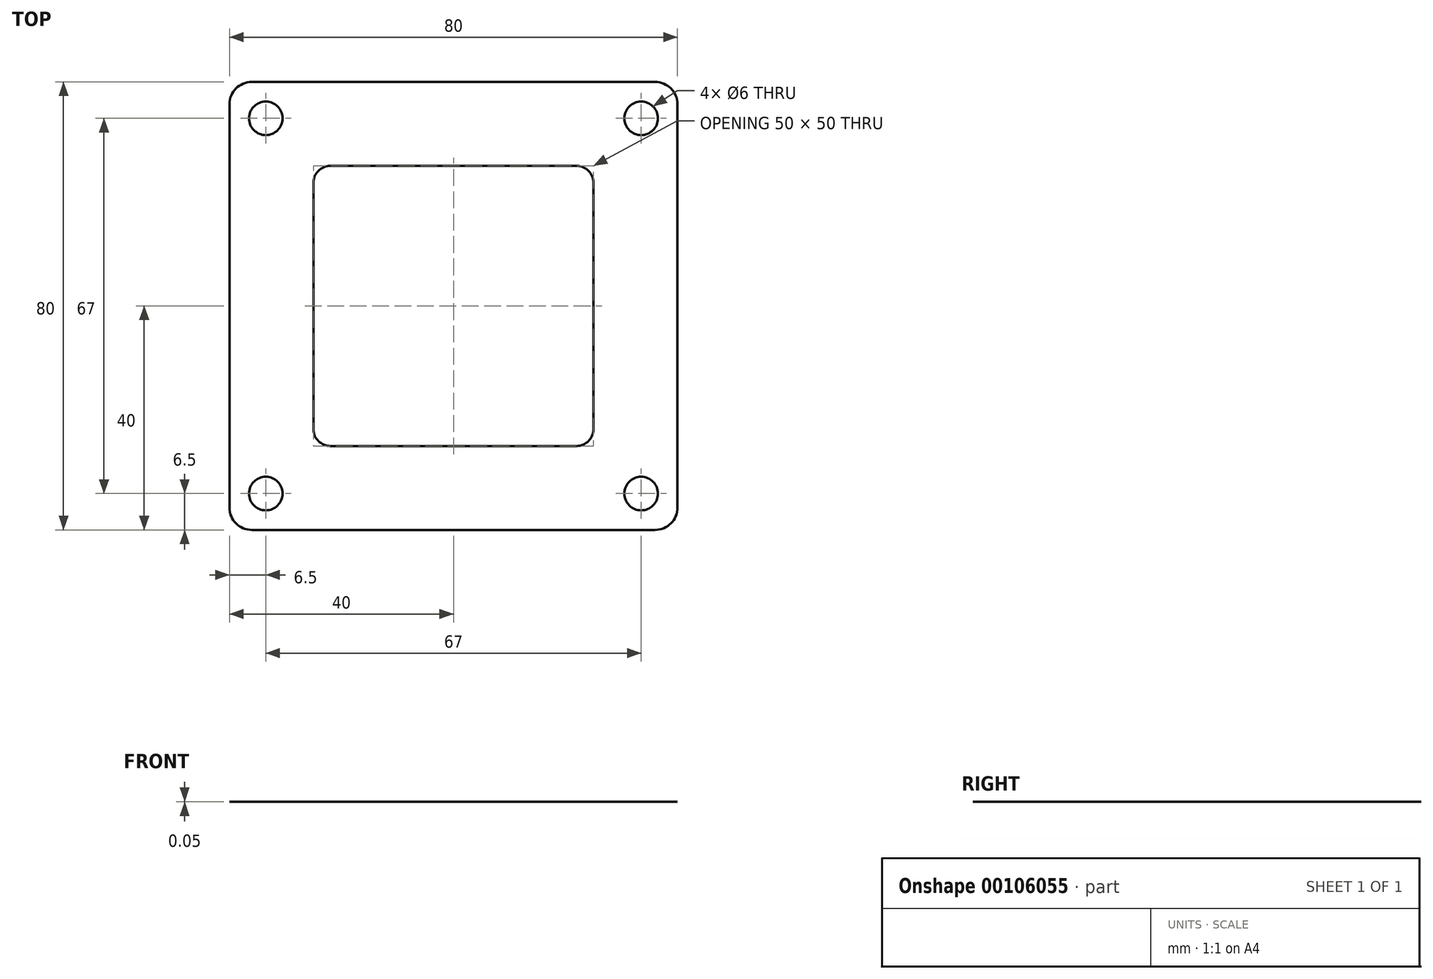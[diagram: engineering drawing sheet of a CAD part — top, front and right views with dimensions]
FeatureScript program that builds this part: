
annotation { "Feature Type Name" : "Feature", "Feature Type Description" : "" }
export const myFeature = defineFeature(function(context is Context, id is Id, definition is map)
    precondition{}
    {
        {
            var Q0;
            Q0=qCreatedBy(makeId("Top.planeOp"),FACE);
            var sketch = newSketch(context, id + "F0", { "sketchPlane" : qUnion([Q0])});
            skLineSegment(sketch, "E0.bottom", {"start": v(4, 0) * mm, "end": v(76, 0) * mm});
            skLineSegment(sketch, "E0.top", {"start": v(4, 80) * mm, "end": v(76, 80) * mm});
            skLineSegment(sketch, "E0.left", {"start": v(0, 4) * mm, "end": v(0, 76) * mm});
            skLineSegment(sketch, "E0.right", {"start": v(80, 4) * mm, "end": v(80, 76) * mm});
            skPoint(sketch, "E1.visualSharp", {"position": v(0, 80) * mm});
            skArc(sketch, "E1.filletArc", {"start": v(4, 80) * mm, "mid": v(1.17, 78.83) * mm, "end": v(0, 76) * mm});
            skPoint(sketch, "E2.visualSharp", {"position": v(80, 80) * mm});
            skArc(sketch, "E2.filletArc", {"start": v(80, 76) * mm, "mid": v(78.83, 78.83) * mm, "end": v(76, 80) * mm});
            skPoint(sketch, "E3.visualSharp", {"position": v(80, 0) * mm});
            skArc(sketch, "E3.filletArc", {"start": v(76, 0) * mm, "mid": v(78.83, 1.17) * mm, "end": v(80, 4) * mm});
            skPoint(sketch, "E4.visualSharp", {"position": v(0, 0) * mm});
            skArc(sketch, "E4.filletArc", {"start": v(0, 4) * mm, "mid": v(1.17, 1.17) * mm, "end": v(4, 0) * mm});
            skLineSegment(sketch, "E5.bottom", {"start": v(18, 65) * mm, "end": v(62, 65) * mm});
            skLineSegment(sketch, "E5.top", {"start": v(18, 15) * mm, "end": v(62, 15) * mm});
            skLineSegment(sketch, "E5.left", {"start": v(15, 62) * mm, "end": v(15, 18) * mm});
            skLineSegment(sketch, "E5.right", {"start": v(65, 62) * mm, "end": v(65, 18) * mm});
            skPoint(sketch, "E6.visualSharp", {"position": v(15, 65) * mm});
            skArc(sketch, "E6.filletArc", {"start": v(18, 65) * mm, "mid": v(15.88, 64.12) * mm, "end": v(15, 62) * mm});
            skPoint(sketch, "E7.visualSharp", {"position": v(65, 65) * mm});
            skArc(sketch, "E7.filletArc", {"start": v(65, 62) * mm, "mid": v(64.12, 64.12) * mm, "end": v(62, 65) * mm});
            skPoint(sketch, "E8.visualSharp", {"position": v(65, 15) * mm});
            skArc(sketch, "E8.filletArc", {"start": v(62, 15) * mm, "mid": v(64.12, 15.88) * mm, "end": v(65, 18) * mm});
            skPoint(sketch, "E9.visualSharp", {"position": v(15, 15) * mm});
            skArc(sketch, "E9.filletArc", {"start": v(15, 18) * mm, "mid": v(15.88, 15.88) * mm, "end": v(18, 15) * mm});
            skCircle(sketch, "E10", {"center": v(6.5, 73.5) * mm, "radius": 3 * mm});
            skCircle(sketch, "E11.0.1.0", {"center": v(6.5, 6.5) * mm, "radius": 3 * mm});
            skCircle(sketch, "E11.1.0.0", {"center": v(73.5, 73.5) * mm, "radius": 3 * mm});
            skCircle(sketch, "E11.1.1.0", {"center": v(73.5, 6.5) * mm, "radius": 3 * mm});
            skLineSegment(sketch, "E11.direction1", {"start": v(6.5, 73.5) * mm, "end": v(73.5, 73.5) * mm, "construction": true});
            skLineSegment(sketch, "E11.direction2", {"start": v(6.5, 73.5) * mm, "end": v(6.5, 6.5) * mm, "construction": true});
            skSolve(sketch);
        }
        {
            var Q0;
            Q0=makeQuery(id+"F0.imprint","IMPRINT",FACE,{"disambiguationData":[TD([[makeQuery(id+"F0.imprint","IMPRINT",EDGE,{"derivedFrom":sQuery(id+"F0.wireOp",EDGE,"E0.bottom")}),1.0]])]});
            extrude(context, id + "F1", {"entities" : qUnion([Q0]), "depth" : 0.05 * mm});
        }
    });
